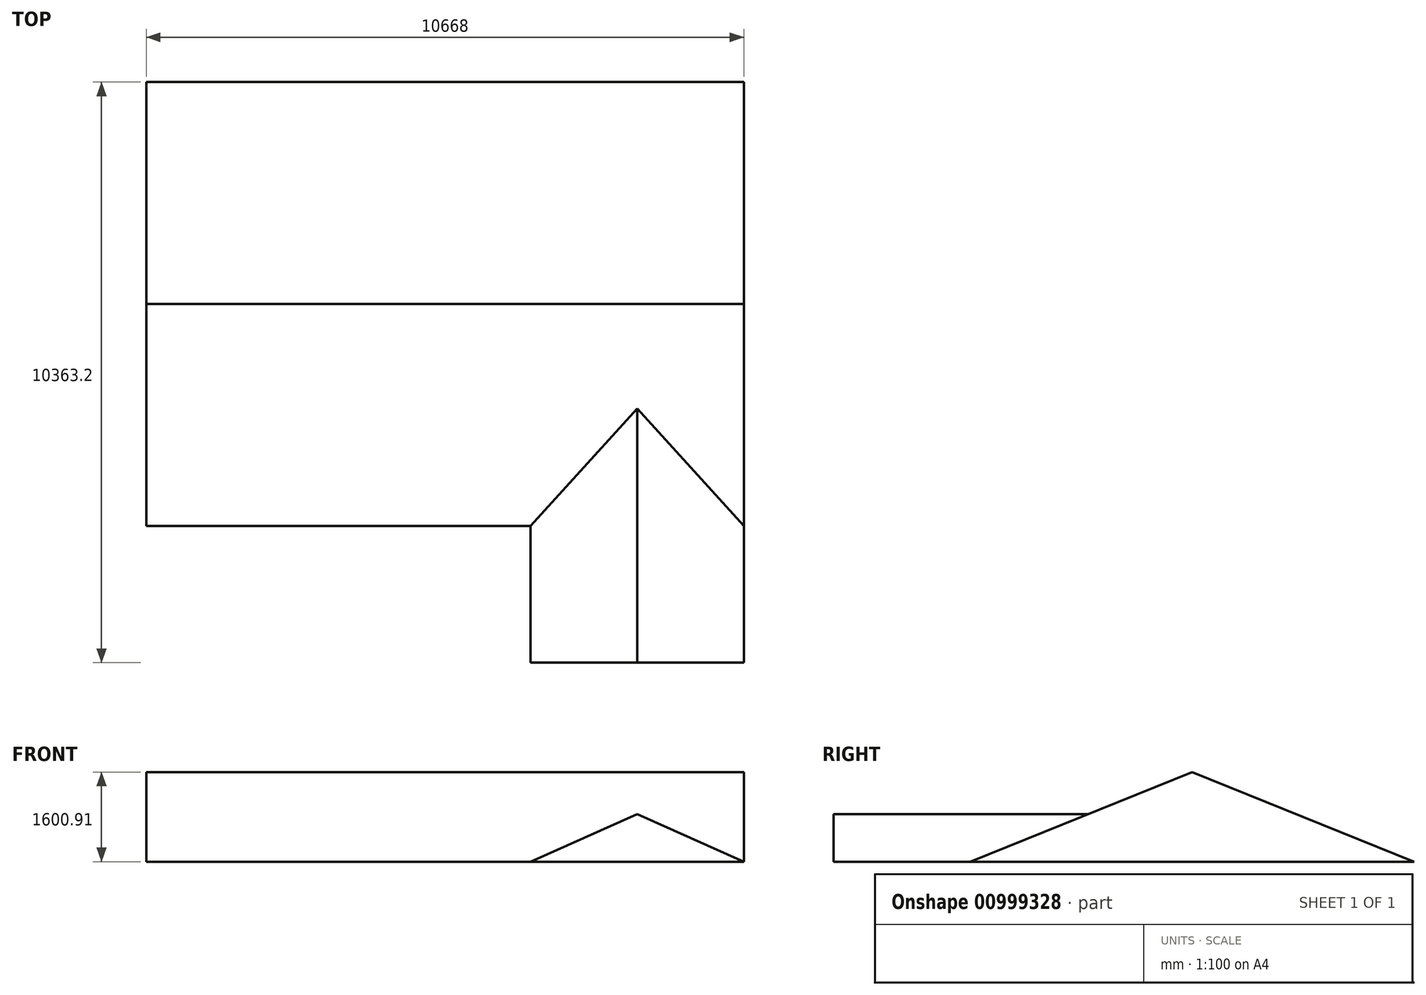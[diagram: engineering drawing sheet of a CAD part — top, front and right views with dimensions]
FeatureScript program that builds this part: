
annotation { "Feature Type Name" : "Feature", "Feature Type Description" : "" }
export const myFeature = defineFeature(function(context is Context, id is Id, definition is map)
    precondition{}
    {
        {
            var Q0;
            Q0=qCreatedBy(makeId("Right.planeOp"),FACE);
            var sketch = newSketch(context, id + "F0", { "sketchPlane" : qUnion([Q0])});
            skLineSegment(sketch, "E0", {"start": v(-3962.4, 0) * mm, "end": v(0, 1600.91) * mm});
            skLineSegment(sketch, "E1", {"start": v(0, 1600.91) * mm, "end": v(3962.4, 0) * mm});
            skLineSegment(sketch, "E2", {"start": v(3962.4, 0) * mm, "end": v(-3962.4, 0) * mm});
            skSolve(sketch);
        }
        {
            var Q0;
            Q0=makeQuery(id+"F0.imprint","IMPRINT",FACE,{"disambiguationData":[TD([[makeQuery(id+"F0.imprint","IMPRINT",EDGE,{"derivedFrom":sQuery(id+"F0.wireOp",EDGE,"E0")}),-1.0]])]});
            extrude(context, id + "F1", {"entities" : qUnion([Q0]), "depth" : 10668 * mm, "offsetDistance" : 25.4 * mm, "symmetric" : true});
        }
        {
            var Q0;
            Q0=qCreatedBy(makeId("Front.planeOp"),FACE);
            cPlane(context, id + "F2", {"entities" : qUnion([Q0]), "cplaneType" : CPlaneType.OFFSET, "offset" : 6400.8 * mm, "width" : 152.4 * mm, "height" : 152.4 * mm});
        }
        {
            var Q0;
            Q0=qCreatedBy(id+"F2.planeOp",FACE);
            var sketch = newSketch(context, id + "F3", { "sketchPlane" : qUnion([Q0])});
            skLineSegment(sketch, "E3", {"start": v(5334, 0) * mm, "end": v(3429, 848.16) * mm});
            skLineSegment(sketch, "E4", {"start": v(3429, 848.16) * mm, "end": v(1524, 0) * mm});
            skLineSegment(sketch, "E5", {"start": v(1524, 0) * mm, "end": v(5334, 0) * mm});
            skPoint(sketch, "E6", {"position": v(3429, 0) * mm});
            skSolve(sketch);
        }
        {
            var Q0;
            Q0 = qSketchRegion(id + "F3", true);
            var Q1;
            Q1=makeQuery(id+"F1.opExtrude","SWEPT_FACE",FACE,{"disambiguationData":[OSD([sQuery(id+"F0.wireOp",EDGE,"E0")])]});
            extrude(context, id + "F4", {"entities" : qUnion([Q0]), "operationType" : NewBodyOperationType.ADD, "endBound" : BoundingType.UP_TO_SURFACE, "oppositeDirection" : true, "depth" : 25.4 * mm, "endBoundEntityFace" : qUnion([Q1]), "offsetDistance" : 25.4 * mm});
        }
    });
